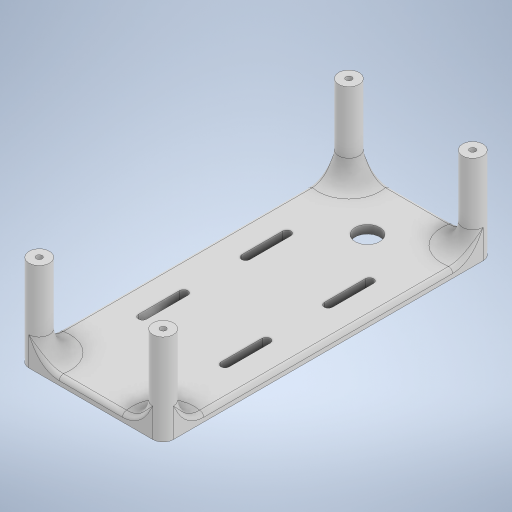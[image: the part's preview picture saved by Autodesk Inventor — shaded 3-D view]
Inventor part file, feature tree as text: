
AUTODESK INVENTOR PART (.ipt)
format: ipt  version: 2023 (Build 270158000, 158)  size: 390,144 bytes
history: native  units: mm
features: sketch x5, extrude x4, mirror x4, fillet x2, hole x1
ambient origin geometry x8: Origin, YZ Plane, XZ Plane, XY Plane, X Axis, Y Axis, Z Axis, Center Point
bodies: Solid1 (feature_tree)
feature tree (16):
  extrude  "Extrusion1"  Depth=70.0mm
  extrude  "Extrusion2"  Depth=5.0mm
  mirror  "Mirror1"
  mirror  "Mirror2"
  fillet  "Fillet1"  Radius=5.0mm
  fillet  "Fillet2"  Radius=4.0mm
  hole  "Hole1"  [1 undecoded]
  extrude  "Extrusion3"  Depth=4.0mm
  mirror  "Mirror3"
  mirror  "Mirror4"
  extrude  "Extrusion4"  Depth=10.0mm
  sketch  "Sketch1"  dims[d0=160.0mm d1=70.0mm]
  sketch  "Sketch2"  dims[d2=5.0mm d3=5.0mm d4=5.0mm d5=4.0mm d6=0.0mm]
  sketch  "Sketch4"  dims[d7=40.0mm d8=0.0mm d9=10.0mm]
  sketch  "Sketch6"  dims[d10=2.0mm]
  sketch  "Sketch7"  dims[d11=2.9mm d12=6.0mm d13=5.5mm d14=2.0mm d15=90.0deg d16=20.0mm d17=20.594885mm d27=4.0mm d28=20.0mm d29=20.0mm d31=25.0mm d32=10.0mm d33=0.0mm d34=12.0mm d35=54.0mm d36=10.0mm d37=0.0mm]
note: 1 required parameter value undecoded (feature->parameter linkage not recoverable at this tier; creation-order binding heuristic only, values carry confidence <= 0.55)
